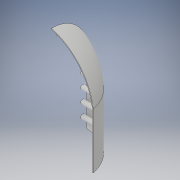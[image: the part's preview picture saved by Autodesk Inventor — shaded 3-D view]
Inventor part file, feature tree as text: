
AUTODESK INVENTOR PART (.ipt)
format: ipt  version: 2019 (Build 230136000, 136)  size: 376,320 bytes
history: native  units: mm
features: sketch x7, projected_geometry x6, extrude x4, other x2, loft x1, shell x1
ambient origin geometry x8: Origin, YZ Plane, XZ Plane, XY Plane, X Axis, Y Axis, Z Axis, Center Point
bodies: Body1 (feature_tree)
feature tree (21):
  other  "правое надкрылье"
  sketch  "Эскиз3"
  sketch  "Эскиз4"
  other  "РабПлоскость1"
  loft  "Лофт1"
  extrude  "Выдавливание2"  Depth=100.0mm
  shell  "Оболочка1"  Thickness=17.0mm
  extrude  "Выдавливание3"  Depth=4.0mm
  extrude  "Выдавливание4"  Depth=35.0mm
  extrude  "Выдавливание5"  TaperAngle=0.0deg  [1 undecoded]
  sketch  "Эскиз5"
  sketch  "Эскиз6"
  projected_geometry  "Спроецированная петля1"
  sketch  "Эскиз7"
  sketch  "Эскиз8"
  sketch  "Эскиз9"
  projected_geometry  "Спроецированная петля2"
  projected_geometry  "Спроецированная петля3"
  projected_geometry  "Спроецированная петля4"
  projected_geometry  "Спроецированная петля5"
  projected_geometry  "Спроецированная петля6"
note: 1 required parameter value undecoded (feature->parameter linkage not recoverable at this tier; creation-order binding heuristic only, values carry confidence <= 0.55)
